# Revit family: VKPD_Eng
name_source: partatom
category: Оборудование
units: mm (PartAtom-declared; Revit-internal decimal feet)

## family parameters
Всегда вертикально = Да
Классификация = Нет
На основе рабочей плоскости = Нет
Общий = Нет
При загрузке вырезать с полостями = Нет
Размер круглого соединителя = Использовать диаметр
Тип детали = Нормальный
Точка принадлежности помещению = Нет

## types (31) — shared parameters
00_20_Manufacturer = Vents
00_20_Name = Duct smoke extraction fan
Casing Material = Metal, painted, blue, matte RAL 5007
Frequency = 50 Гц
Load Classification = HVAC
Maintenance zone material = <По категории>
URL = https://ventilation-system.com
Изготовитель = Vents
zero-valued in all types: Height, Length, Width, Отметка по умолчанию

## per-type parameters (varying)
| type | A | A1 | A2 | B | B1 | B2 | C | D | D1 | D2 | D3 | Hole | Maximum Air Flow | Motor | Number of Fase | Power | Voltage | Weight | b | b1 | c | r |
| VKPD-250-2E/0,37-500х300 | 500 мм | 520 мм | 540 мм | 300 мм | 320 мм | 340 мм | 680 мм | 557 мм | 200 мм | 160 мм | 120 мм | Нет | 2300.0 м³/ч | Motor : Motor_250 | 1 | 370 Вт | 230 В | 40.00 кг | 135 мм | 100 мм | 322 мм | 17 мм |
| VKPD-710-4D/7,5-1200x900 | 1200 мм | 1220 мм | 1240 мм | 900 мм | 920 мм | 940 мм | 1040 мм | 1354 мм | 480 мм | 384 мм | 288 мм | Да | 27720.0 м³/ч | Motor : Motor_710 | 3 | 7500 Вт | 400 В | 178.00 кг | 405 мм | 300 мм | 466 мм | 40 мм |
| VKPD-280-2E/0,55-600x300 | 600 мм | 620 мм | 640 мм | 300 мм | 320 мм | 340 мм | 680 мм | 558 мм | 240 мм | 192 мм | 144 мм | Нет | 3150.0 м³/ч | Motor : Motor_280 | 1 | 550 Вт | 230 В | 40.00 кг | 135 мм | 100 мм | 322 мм | 20 мм |
| VKPD-315-2E/1,1-600x350 | 600 мм | 620 мм | 640 мм | 350 мм | 370 мм | 390 мм | 680 мм | 624 мм | 240 мм | 192 мм | 144 мм | Нет | 4608.0 м³/ч | Motor : Motor_315 | 1 | 1100 Вт | 230 В | 56.00 кг | 158 мм | 117 мм | 322 мм | 20 мм |
| VKPD-355-4E/0,37-700x400 | 700 мм | 720 мм | 740 мм | 400 мм | 420 мм | 440 мм | 680 мм | 657 мм | 280 мм | 224 мм | 168 мм | Да | 3294.0 м³/ч | Motor : Motor_280 | 1 | 370 Вт | 230 В | 51.00 кг | 180 мм | 133 мм | 322 мм | 23 мм |
| VKPD-400-4E/0,55-700x500 | 700 мм | 720 мм | 740 мм | 500 мм | 520 мм | 540 мм | 680 мм | 772 мм | 280 мм | 224 мм | 168 мм | Да | 4500.0 м³/ч | Motor : Motor_400 | 1 | 550 Вт | 230 В | 70.00 кг | 225 мм | 167 мм | 322 мм | 23 мм |
| VKPD-450-4E/0,75-800х600 | 800 мм | 820 мм | 840 мм | 600 мм | 620 мм | 640 мм | 800 мм | 872 мм | 320 мм | 256 мм | 192 мм | Да | 6768.0 м³/ч | Motor : Motor_450 | 1 | 750 Вт | 230 В | 89.00 кг | 270 мм | 200 мм | 370 мм | 27 мм |
| VKPD-500-4E/1,5-800х600 | 800 мм | 820 мм | 840 мм | 600 мм | 620 мм | 640 мм | 840 мм | 914 мм | 320 мм | 256 мм | 192 мм | Да | 9720.0 м³/ч | Motor : Motor_500 | 1 | 1500 Вт | 230 В | 97.00 кг | 270 мм | 200 мм | 386 мм | 27 мм |
| VKPD-560-4E/3-900х700 | 900 мм | 920 мм | 940 мм | 700 мм | 720 мм | 740 мм | 840 мм | 1058 мм | 360 мм | 288 мм | 216 мм | Да | 13680.0 м³/ч | Motor : Motor_560 | 1 | 3000 Вт | 230 В | 100.00 кг | 315 мм | 233 мм | 386 мм | 30 мм |
| VKPD-630-4D/4-1000х800 | 1000 мм | 1020 мм | 1040 мм | 800 мм | 820 мм | 840 мм | 1040 мм | 1150 мм | 400 мм | 320 мм | 240 мм | Да | 18540.0 м³/ч | Motor : Motor_630 | 3 | 4000 Вт | 400 В | 130.00 кг | 360 мм | 267 мм | 466 мм | 33 мм |
| VKPD-250-2D/0,37-500х300 | 500 мм | 520 мм | 540 мм | 300 мм | 320 мм | 340 мм | 680 мм | 557 мм | 200 мм | 160 мм | 120 мм | Нет | 2300.0 м³/ч | Motor : Motor_250 | 3 | 370 Вт | 400 В | 40.00 кг | 135 мм | 100 мм | 322 мм | 17 мм |
| VKPD-250-2/4D/0,37/0,1-500х300 | 500 мм | 520 мм | 540 мм | 300 мм | 320 мм | 340 мм | 680 мм | 557 мм | 200 мм | 160 мм | 120 мм | Нет | 2300.0 м³/ч | Motor : Motor_250 | 3 | 370 Вт | 400 В | 40.00 кг | 135 мм | 100 мм | 322 мм | 17 мм |
| VKPD-280-2D/0,55-600x300 | 600 мм | 620 мм | 640 мм | 300 мм | 320 мм | 340 мм | 680 мм | 558 мм | 240 мм | 192 мм | 144 мм | Нет | 3150.0 м³/ч | Motor : Motor_280 | 3 | 550 Вт | 400 В | 40.00 кг | 135 мм | 100 мм | 322 мм | 20 мм |
| VKPD-280-2/4D/0,55/0,1-600x300 | 600 мм | 620 мм | 640 мм | 300 мм | 320 мм | 340 мм | 680 мм | 558 мм | 240 мм | 192 мм | 144 мм | Нет | 3150.0 м³/ч | Motor : Motor_280 | 3 | 550 Вт | 400 В | 40.00 кг | 135 мм | 100 мм | 322 мм | 20 мм |
| VKPD-315-2D/1,1-600x350 | 600 мм | 620 мм | 640 мм | 350 мм | 370 мм | 390 мм | 680 мм | 624 мм | 240 мм | 192 мм | 144 мм | Нет | 4608.0 м³/ч | Motor : Motor_315 | 3 | 1100 Вт | 400 В | 56.00 кг | 158 мм | 117 мм | 322 мм | 20 мм |
| VKPD-315-2/4D/1,1/0,25-600x350 | 600 мм | 620 мм | 640 мм | 350 мм | 370 мм | 390 мм | 680 мм | 624 мм | 240 мм | 192 мм | 144 мм | Нет | 4608.0 м³/ч | Motor : Motor_315 | 3 | 1100 Вт | 400 В | 56.00 кг | 158 мм | 117 мм | 322 мм | 20 мм |
| VKPD-355-4D/0,37-700x400 | 700 мм | 720 мм | 740 мм | 400 мм | 420 мм | 440 мм | 680 мм | 657 мм | 280 мм | 224 мм | 168 мм | Да | 3294.0 м³/ч | Motor : Motor_280 | 3 | 370 Вт | 400 В | 51.00 кг | 180 мм | 133 мм | 322 мм | 23 мм |
| VKPD-355-4/6D/0,55/0,1-700x400 | 700 мм | 720 мм | 740 мм | 400 мм | 420 мм | 440 мм | 680 мм | 657 мм | 280 мм | 224 мм | 168 мм | Да | 3294.0 м³/ч | Motor : Motor_280 | 3 | 550 Вт | 400 В | 51.00 кг | 180 мм | 133 мм | 322 мм | 23 мм |
| VKPD-400-4D/0,55-700x500 | 700 мм | 720 мм | 740 мм | 500 мм | 520 мм | 540 мм | 680 мм | 772 мм | 280 мм | 224 мм | 168 мм | Да | 4500.0 м³/ч | Motor : Motor_400 | 3 | 550 Вт | 400 В | 70.00 кг | 225 мм | 167 мм | 322 мм | 23 мм |
| VKPD-400-4/6D/0,55/0,25-700x500 | 700 мм | 720 мм | 740 мм | 500 мм | 520 мм | 540 мм | 680 мм | 772 мм | 280 мм | 224 мм | 168 мм | Да | 4500.0 м³/ч | Motor : Motor_400 | 3 | 550 Вт | 400 В | 70.00 кг | 225 мм | 167 мм | 322 мм | 23 мм |
| VKPD-450-4D/0,75-800х600 | 800 мм | 820 мм | 840 мм | 600 мм | 620 мм | 640 мм | 800 мм | 872 мм | 320 мм | 256 мм | 192 мм | Да | 6768.0 м³/ч | Motor : Motor_450 | 3 | 750 Вт | 400 В | 89.00 кг | 270 мм | 200 мм | 370 мм | 27 мм |
| VKPD-450-4/6D/0,8/0,2-800х600 | 800 мм | 820 мм | 840 мм | 600 мм | 620 мм | 640 мм | 800 мм | 872 мм | 320 мм | 256 мм | 192 мм | Да | 6768.0 м³/ч | Motor : Motor_450 | 3 | 800 Вт | 400 В | 89.00 кг | 270 мм | 200 мм | 370 мм | 27 мм |
| VKPD-500-4D/1,5-800х600 | 800 мм | 820 мм | 840 мм | 600 мм | 620 мм | 640 мм | 840 мм | 914 мм | 320 мм | 256 мм | 192 мм | Да | 9720.0 м³/ч | Motor : Motor_500 | 3 | 1500 Вт | 400 В | 97.00 кг | 270 мм | 200 мм | 386 мм | 27 мм |
| VKPD-500-4/6D/1,5/0,37-800х600 | 800 мм | 820 мм | 840 мм | 600 мм | 620 мм | 640 мм | 840 мм | 914 мм | 320 мм | 256 мм | 192 мм | Да | 9720.0 м³/ч | Motor : Motor_500 | 3 | 1500 Вт | 400 В | 97.00 кг | 270 мм | 200 мм | 386 мм | 27 мм |
| VKPD-560-4D/3-900х700 | 900 мм | 920 мм | 940 мм | 700 мм | 720 мм | 740 мм | 840 мм | 1058 мм | 360 мм | 288 мм | 216 мм | Да | 13680.0 м³/ч | Motor : Motor_560 | 3 | 3000 Вт | 400 В | 100.00 кг | 315 мм | 233 мм | 386 мм | 30 мм |
| VKPD-560-4/6D/2,8/0,7-900х700 | 900 мм | 920 мм | 940 мм | 700 мм | 720 мм | 740 мм | 840 мм | 1058 мм | 360 мм | 288 мм | 216 мм | Да | 13680.0 м³/ч | Motor : Motor_560 | 3 | 2800 Вт | 400 В | 100.00 кг | 315 мм | 233 мм | 386 мм | 30 мм |
| VKPD-560-4/8D/2,8/0,55-900x700 | 900 мм | 920 мм | 940 мм | 700 мм | 720 мм | 740 мм | 840 мм | 1058 мм | 360 мм | 288 мм | 216 мм | Да | 13680.0 м³/ч | Motor : Motor_560 | 3 | 2800 Вт | 400 В | 100.00 кг | 315 мм | 233 мм | 386 мм | 30 мм |
| VKPD-630-4/6D/3,8/1-1000х800 | 1000 мм | 1020 мм | 1040 мм | 800 мм | 820 мм | 840 мм | 1040 мм | 1150 мм | 400 мм | 320 мм | 240 мм | Да | 18540.0 м³/ч | Motor : Motor_630 | 3 | 3800 Вт | 400 В | 130.00 кг | 360 мм | 267 мм | 466 мм | 33 мм |
| VKPD-630-4/8D/3,8/0,75-1000x800 | 1000 мм | 1020 мм | 1040 мм | 800 мм | 820 мм | 840 мм | 1040 мм | 1150 мм | 400 мм | 320 мм | 240 мм | Да | 18540.0 м³/ч | Motor : Motor_630 | 3 | 3800 Вт | 400 В | 130.00 кг | 360 мм | 267 мм | 466 мм | 33 мм |
| VKPD-710-4/6D/7,5/2,2-1200x900 | 1200 мм | 1220 мм | 1240 мм | 900 мм | 920 мм | 940 мм | 1040 мм | 1354 мм | 480 мм | 384 мм | 288 мм | Да | 27720.0 м³/ч | Motor : Motor_710 | 3 | 7500 Вт | 400 В | 178.00 кг | 405 мм | 300 мм | 466 мм | 40 мм |
| VKPD-710-4/8D/7,5/1-1200x900 | 1200 мм | 1220 мм | 1240 мм | 900 мм | 920 мм | 940 мм | 1040 мм | 1354 мм | 480 мм | 384 мм | 288 мм | Да | 27720.0 м³/ч | Motor : Motor_710 | 3 | 7500 Вт | 400 В | 178.00 кг | 405 мм | 300 мм | 466 мм | 40 мм |

note: column(s) folded — value = type name in every type: 00_20_Type
